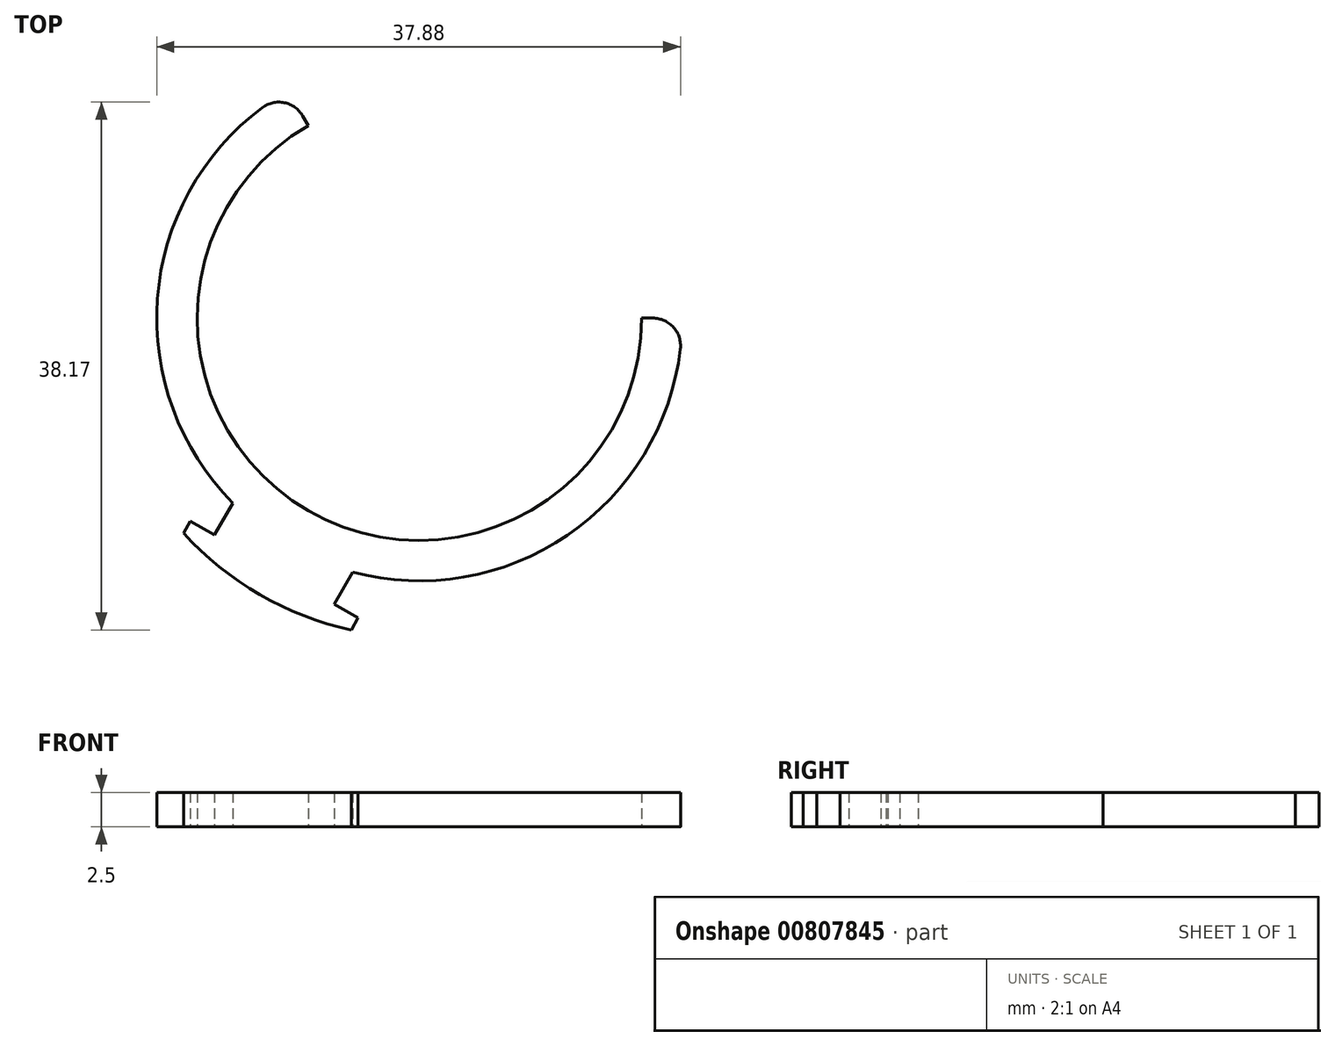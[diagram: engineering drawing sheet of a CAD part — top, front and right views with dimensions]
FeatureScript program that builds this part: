
annotation { "Feature Type Name" : "Feature", "Feature Type Description" : "" }
export const myFeature = defineFeature(function(context is Context, id is Id, definition is map)
    precondition{}
    {
        {
            var Q0;
            Q0=qCreatedBy(makeId("Top.planeOp"),FACE);
            var sketch = newSketch(context, id + "F0", { "sketchPlane" : qUnion([Q0])});
            skCircle(sketch, "E0", {"center": v(0, 0) * mm, "radius": 15.88 * mm, "construction": true});
            skArc(sketch, "E1", {"start": v(-9.5, 16.45) * mm, "mid": v(-9.5, -16.45) * mm, "end": v(19, 0) * mm});
            skArc(sketch, "E2.0", {"start": v(-8.04, 13.92) * mm, "mid": v(-8.04, -13.92) * mm, "end": v(16.07, 0) * mm});
            skLineSegment(sketch, "E3", {"start": v(0, 0) * mm, "end": v(19, 0) * mm});
            skLineSegment(sketch, "E4", {"start": v(0, 0) * mm, "end": v(-9.5, 16.45) * mm});
            skLineSegment(sketch, "E5", {"start": v(0, 0) * mm, "end": v(-9.5, -16.45) * mm, "construction": true});
            skLineSegment(sketch, "E6", {"start": v(-13.83, -13.95) * mm, "end": v(-5.17, -18.95) * mm, "construction": true});
            skPoint(sketch, "E7", {"position": v(-9.5, -16.45) * mm});
            skLineSegment(sketch, "E8", {"start": v(-5.17, -18.95) * mm, "end": v(-6.17, -20.69) * mm});
            skLineSegment(sketch, "E9", {"start": v(-6.17, -20.69) * mm, "end": v(-4.44, -21.69) * mm});
            skLineSegment(sketch, "E10", {"start": v(-4.44, -21.69) * mm, "end": v(-4.94, -22.55) * mm});
            skArc(sketch, "E11", {"start": v(-17.06, -15.55) * mm, "mid": v(-11.54, -20) * mm, "end": v(-4.94, -22.55) * mm});
            skLineSegment(sketch, "E12.MirrorCS", {"start": v(-13.83, -13.95) * mm, "end": v(-14.83, -15.69) * mm});
            skLineSegment(sketch, "E13.MirrorCS", {"start": v(-14.83, -15.69) * mm, "end": v(-16.56, -14.69) * mm});
            skLineSegment(sketch, "E14.MirrorCS", {"start": v(-16.56, -14.69) * mm, "end": v(-17.06, -15.55) * mm});
            skLineSegment(sketch, "E15", {"start": v(-5.17, -18.95) * mm, "end": v(-4.84, -18.37) * mm});
            skLineSegment(sketch, "E16.MirrorCS", {"start": v(-13.83, -13.95) * mm, "end": v(-13.5, -13.37) * mm});
            skSolve(sketch);
        }
        {
            var Q0;
            {var subQ0=sQuery(id+"F0.wireOp",EDGE,"E1");Q0=makeQuery(id+"F0.imprint","IMPRINT",FACE,{"disambiguationData":[TD([[makeQuery(id+"F0.imprint","IMPRINT",EDGE,{"derivedFrom":subQ0}),1.0]])]});}
            var Q1;
            Q1=makeQuery(id+"F0.imprint","IMPRINT",FACE,{"disambiguationData":[TD([[makeQuery(id+"F0.imprint","IMPRINT",EDGE,{"derivedFrom":sQuery(id+"F0.wireOp",EDGE,"E8")}),-1.0]])]});
            extrude(context, id + "F1", {"entities" : qUnion([Q0, Q1]), "depth" : 2.5 * mm, "offsetDistance" : 25 * mm});
        }
        {
            var Q0;
            Q0=makeQuery(id+"F1.opExtrude","SWEPT_EDGE",EDGE,{"disambiguationData":[OSD([sQuery(id+"F0.wireOp",EDGE,"E1"),sQuery(id+"F0.wireOp",EDGE,"E3")])]});
            var Q1;
            Q1=makeQuery(id+"F1.opExtrude","SWEPT_EDGE",EDGE,{"disambiguationData":[OSD([sQuery(id+"F0.wireOp",EDGE,"E1"),sQuery(id+"F0.wireOp",EDGE,"E4")])]});
            fillet(context, id + "F2", {"entities" : qUnion([Q0, Q1]), "radius" : 2 * mm, "tangentPropagation" : true, "allowEdgeOverflow" : false});
        }
    });
